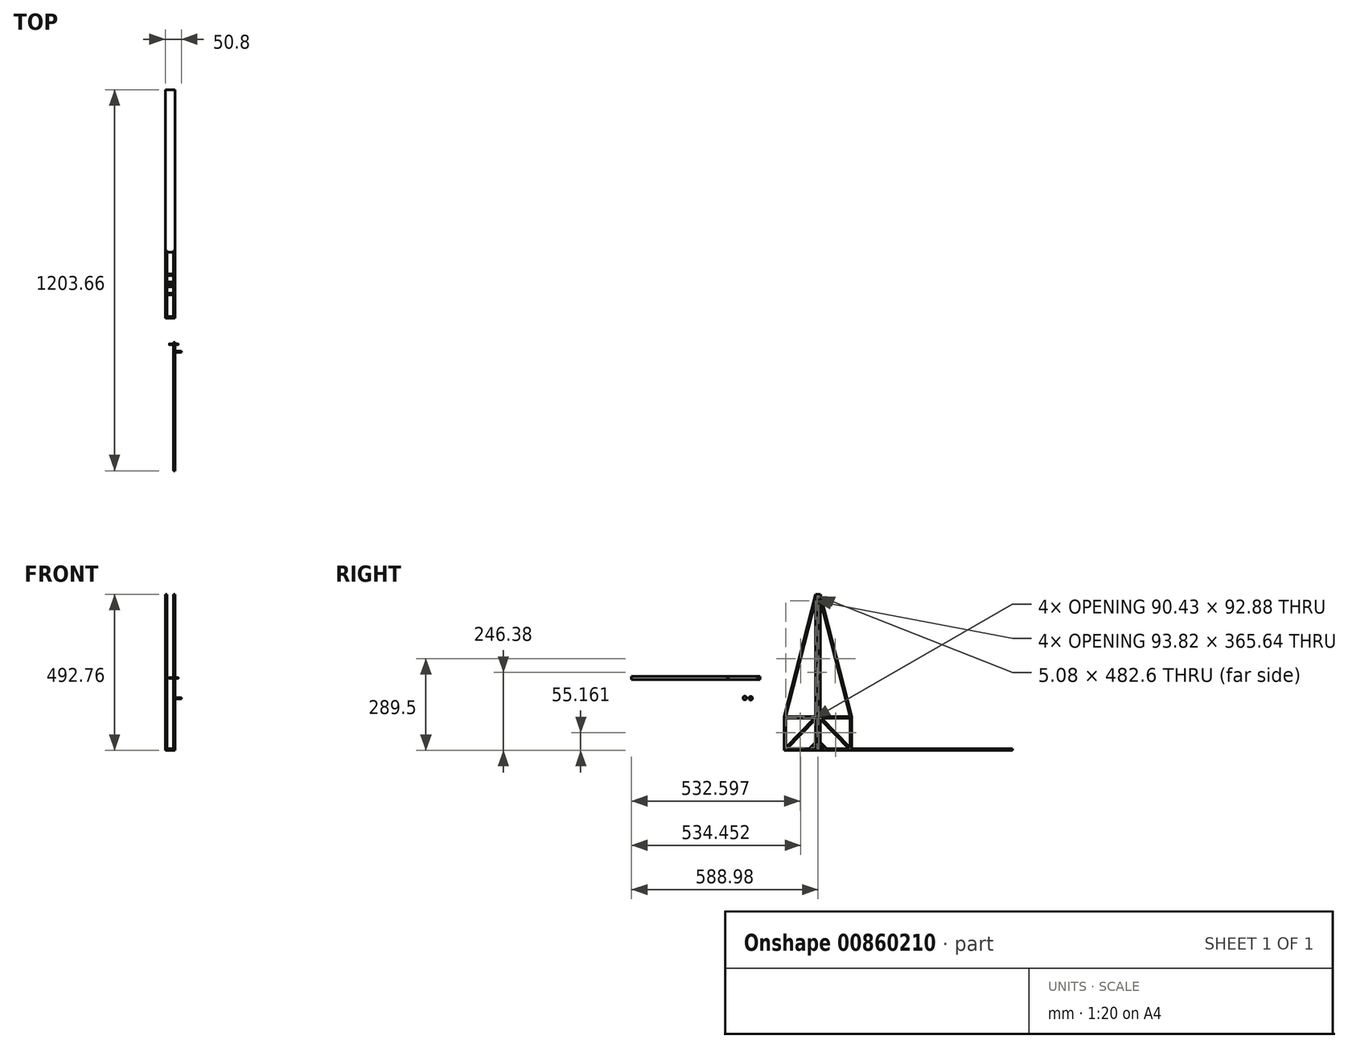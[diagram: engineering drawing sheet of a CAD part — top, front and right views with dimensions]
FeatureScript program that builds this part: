
annotation { "Feature Type Name" : "Feature", "Feature Type Description" : "" }
export const myFeature = defineFeature(function(context is Context, id is Id, definition is map)
    precondition{}
    {
        {
            var Q0;
            Q0=qCreatedBy(makeId("Right.planeOp"),FACE);
            var sketch = newSketch(context, id + "F0", { "sketchPlane" : qUnion([Q0])});
            skLineSegment(sketch, "E0.bottom", {"start": v(0, 0) * mm, "end": v(101.6, 0) * mm});
            skLineSegment(sketch, "E0.top", {"start": v(0, -101.6) * mm, "end": v(101.6, -101.6) * mm});
            skLineSegment(sketch, "E0.left", {"start": v(0, 0) * mm, "end": v(0, -101.6) * mm});
            skLineSegment(sketch, "E0.right", {"start": v(101.6, 0) * mm, "end": v(101.6, -101.6) * mm});
            skLineSegment(sketch, "E1.bottom", {"start": v(0, 0) * mm, "end": v(-101.6, 0) * mm});
            skLineSegment(sketch, "E1.top", {"start": v(0, -101.6) * mm, "end": v(-101.6, -101.6) * mm});
            skLineSegment(sketch, "E1.right", {"start": v(-101.6, 0) * mm, "end": v(-101.6, -101.6) * mm});
            skLineSegment(sketch, "E2.0", {"start": v(106.68, 0) * mm, "end": v(106.68, -106.68) * mm});
            skLineSegment(sketch, "E2.1", {"start": v(0, -106.68) * mm, "end": v(106.68, -106.68) * mm});
            skLineSegment(sketch, "E2.2", {"start": v(0, -106.68) * mm, "end": v(-106.68, -106.68) * mm});
            skLineSegment(sketch, "E2.3", {"start": v(-106.68, 0) * mm, "end": v(-106.68, -106.68) * mm});
            skLineSegment(sketch, "E3.0", {"start": v(0, -5.08) * mm, "end": v(101.6, -5.08) * mm});
            skLineSegment(sketch, "E3.1", {"start": v(0, -5.08) * mm, "end": v(-101.6, -5.08) * mm});
            skLineSegment(sketch, "E4", {"start": v(-106.68, 0) * mm, "end": v(-101.6, 0) * mm});
            skLineSegment(sketch, "E5", {"start": v(101.6, 0) * mm, "end": v(106.68, 0) * mm});
            skLineSegment(sketch, "E6.0", {"start": v(2.54, 0) * mm, "end": v(2.54, 381) * mm});
            skLineSegment(sketch, "E7.0", {"start": v(-2.54, 0) * mm, "end": v(-2.54, 381) * mm});
            skLineSegment(sketch, "E8", {"start": v(-2.54, 381) * mm, "end": v(2.54, 381) * mm});
            skLineSegment(sketch, "E9", {"start": v(2.54, 381) * mm, "end": v(7.62, 381) * mm});
            skLineSegment(sketch, "E10", {"start": v(7.62, 381) * mm, "end": v(7.62, 0) * mm});
            skLineSegment(sketch, "E11.0", {"start": v(-7.62, 0) * mm, "end": v(-7.62, 381) * mm});
            skLineSegment(sketch, "E12", {"start": v(-7.62, 381) * mm, "end": v(-2.54, 381) * mm});
            skLineSegment(sketch, "E13", {"start": v(-7.62, 381) * mm, "end": v(-7.62, 386.08) * mm});
            skLineSegment(sketch, "E14", {"start": v(-7.62, 386.08) * mm, "end": v(7.62, 386.08) * mm});
            skLineSegment(sketch, "E15", {"start": v(7.62, 386.08) * mm, "end": v(7.62, 381) * mm});
            skLineSegment(sketch, "E16", {"start": v(-2.54, 0) * mm, "end": v(-2.54, -101.6) * mm});
            skLineSegment(sketch, "E17", {"start": v(-7.62, 0) * mm, "end": v(-7.62, -101.6) * mm});
            skLineSegment(sketch, "E18", {"start": v(2.54, 0) * mm, "end": v(2.54, -101.6) * mm});
            skLineSegment(sketch, "E19", {"start": v(7.62, 0) * mm, "end": v(7.62, -101.6) * mm});
            skLineSegment(sketch, "E20", {"start": v(-7.62, -101.6) * mm, "end": v(-7.62, -88.9) * mm});
            skLineSegment(sketch, "E21", {"start": v(-7.62, -101.6) * mm, "end": v(-20.32, -101.6) * mm});
            skLineSegment(sketch, "E22", {"start": v(-20.32, -101.6) * mm, "end": v(-7.62, -88.9) * mm});
            skLineSegment(sketch, "E23.0", {"start": v(-23.91, -98) * mm, "end": v(-11.21, -85.3) * mm});
            skLineSegment(sketch, "E24", {"start": v(-23.91, -98) * mm, "end": v(-27.5, -101.6) * mm});
            skLineSegment(sketch, "E25", {"start": v(-11.21, -85.3) * mm, "end": v(-7.62, -81.72) * mm});
            skLineSegment(sketch, "E26.MirrorCS", {"start": v(23.91, -98) * mm, "end": v(27.5, -101.6) * mm});
            skLineSegment(sketch, "E27.MirrorCS", {"start": v(23.91, -98) * mm, "end": v(11.21, -85.3) * mm});
            skLineSegment(sketch, "E28.MirrorCS", {"start": v(20.32, -101.6) * mm, "end": v(7.62, -88.9) * mm});
            skLineSegment(sketch, "E29.MirrorCS", {"start": v(11.21, -85.3) * mm, "end": v(7.62, -81.72) * mm});
            skLineSegment(sketch, "E30", {"start": v(-7.62, 386.08) * mm, "end": v(-106.68, 0) * mm});
            skPoint(sketch, "E31", {"position": v(-7.62, 365.64) * mm});
            skPoint(sketch, "E32", {"position": v(-101.44, 0) * mm});
            skLineSegment(sketch, "E33", {"start": v(-101.44, 0) * mm, "end": v(-7.62, 365.64) * mm});
            skLineSegment(sketch, "E34.MirrorCS", {"start": v(101.44, 0) * mm, "end": v(7.62, 365.64) * mm});
            skLineSegment(sketch, "E35.MirrorCS", {"start": v(7.62, 386.08) * mm, "end": v(106.68, 0) * mm});
            skPoint(sketch, "E36", {"position": v(-101.6, -97.96) * mm});
            skPoint(sketch, "E37", {"position": v(-98.05, -101.6) * mm});
            skPoint(sketch, "E38", {"position": v(-7.62, -8.72) * mm});
            skPoint(sketch, "E39", {"position": v(-11.17, -5.08) * mm});
            skLineSegment(sketch, "E40", {"start": v(-7.62, -8.72) * mm, "end": v(-98.05, -101.6) * mm});
            skLineSegment(sketch, "E41", {"start": v(-101.6, -97.96) * mm, "end": v(-11.17, -5.08) * mm});
            skLineSegment(sketch, "E42.MirrorCS", {"start": v(101.6, -97.96) * mm, "end": v(11.17, -5.08) * mm});
            skLineSegment(sketch, "E43.MirrorCS", {"start": v(7.62, -8.72) * mm, "end": v(98.05, -101.6) * mm});
            skSolve(sketch);
        }
        {
            var Q0;
            Q0=makeQuery(id+"F0.imprint","IMPRINT",FACE,{"disambiguationData":[TD([[makeQuery(id+"F0.imprint","IMPRINT",EDGE,{"derivedFrom":sQuery(id+"F0.wireOp",EDGE,"E2.0")}),-1.0]])]});
            var Q1;
            {var subQ0=sQuery(id+"F0.wireOp",EDGE,"E3.0");var subQ1=sQuery(id+"F0.wireOp",EDGE,"E0.right");var subQ2=makeQuery(id+"F0.imprint","INTERSECT",VERTEX,{"derivedFrom":[subQ1,subQ0]});Q1=makeQuery(id+"F0.imprint","IMPRINT",FACE,{"disambiguationData":[TD([[makeQuery(id+"F0.imprint","IMPRINT",EDGE,{"disambiguationData":[TD([[subQ2,1.0]])],"derivedFrom":subQ0}),1.0]])]});}
            var Q2;
            {var subQ0=sQuery(id+"F0.wireOp",EDGE,"E3.1");var subQ1=sQuery(id+"F0.wireOp",EDGE,"E1.right");var subQ2=makeQuery(id+"F0.imprint","INTERSECT",VERTEX,{"derivedFrom":[subQ1,subQ0]});Q2=makeQuery(id+"F0.imprint","IMPRINT",FACE,{"disambiguationData":[TD([[makeQuery(id+"F0.imprint","IMPRINT",EDGE,{"disambiguationData":[TD([[subQ2,1.0]])],"derivedFrom":subQ0}),-1.0]])]});}
            var Q3;
            {var subQ4=sQuery(id+"F0.wireOp",EDGE,"E6.0");Q3=makeQuery(id+"F0.imprint","IMPRINT",FACE,{"disambiguationData":[TD([[makeQuery(id+"F0.imprint","IMPRINT",EDGE,{"derivedFrom":subQ4}),-1.0]])]});}
            var Q4;
            {var subQ5=sQuery(id+"F0.wireOp",EDGE,"E7.0");Q4=makeQuery(id+"F0.imprint","IMPRINT",FACE,{"disambiguationData":[TD([[makeQuery(id+"F0.imprint","IMPRINT",EDGE,{"derivedFrom":subQ5}),1.0]])]});}
            var Q5;
            Q5=makeQuery(id+"F0.imprint","IMPRINT",FACE,{"disambiguationData":[TD([[makeQuery(id+"F0.imprint","IMPRINT",EDGE,{"derivedFrom":sQuery(id+"F0.wireOp",EDGE,"E8")}),1.0]])]});
            var Q6;
            {var subQ3=sQuery(id+"F0.wireOp",EDGE,"E16");var subQ4=sQuery(id+"F0.wireOp",EDGE,"E1.top");var subQ5=makeQuery(id+"F0.imprint","INTERSECT",VERTEX,{"derivedFrom":[subQ4,subQ3]});Q6=makeQuery(id+"F0.imprint","IMPRINT",FACE,{"disambiguationData":[TD([[makeQuery(id+"F0.imprint","IMPRINT",EDGE,{"disambiguationData":[TD([[subQ5,-1.0]])],"derivedFrom":subQ4}),-1.0]])]});}
            var Q7;
            {var subQ0=sQuery(id+"F0.wireOp",EDGE,"E40");Q7=makeQuery(id+"F0.imprint","IMPRINT",FACE,{"disambiguationData":[TD([[makeQuery(id+"F0.imprint","IMPRINT",EDGE,{"derivedFrom":subQ0}),-1.0]])]});}
            var Q8;
            {var subQ3=sQuery(id+"F0.wireOp",EDGE,"E18");var subQ5=sQuery(id+"F0.wireOp",EDGE,"E3.0");var subQ7=makeQuery(id+"F0.imprint","INTERSECT",VERTEX,{"derivedFrom":[subQ5,subQ3]});Q8=makeQuery(id+"F0.imprint","IMPRINT",FACE,{"disambiguationData":[TD([[makeQuery(id+"F0.imprint","IMPRINT",EDGE,{"disambiguationData":[TD([[subQ7,-1.0]])],"derivedFrom":subQ5}),1.0]])]});}
            var Q9;
            {var subQ3=sQuery(id+"F0.wireOp",EDGE,"E16");var subQ5=sQuery(id+"F0.wireOp",EDGE,"E3.1");var subQ6=makeQuery(id+"F0.imprint","INTERSECT",VERTEX,{"derivedFrom":[subQ5,subQ3]});Q9=makeQuery(id+"F0.imprint","IMPRINT",FACE,{"disambiguationData":[TD([[makeQuery(id+"F0.imprint","IMPRINT",EDGE,{"disambiguationData":[TD([[subQ6,-1.0]])],"derivedFrom":subQ5}),-1.0]])]});}
            var Q10;
            {var subQ0=sQuery(id+"F0.wireOp",EDGE,"E18");var subQ1=sQuery(id+"F0.wireOp",EDGE,"E0.top");var subQ2=makeQuery(id+"F0.imprint","INTERSECT",VERTEX,{"derivedFrom":[subQ1,subQ0]});Q10=makeQuery(id+"F0.imprint","IMPRINT",FACE,{"disambiguationData":[TD([[makeQuery(id+"F0.imprint","IMPRINT",EDGE,{"disambiguationData":[TD([[subQ2,-1.0]])],"derivedFrom":subQ1}),1.0]])]});}
            var Q11;
            {var subQ4=sQuery(id+"F0.wireOp",EDGE,"E42.MirrorCS");Q11=makeQuery(id+"F0.imprint","IMPRINT",FACE,{"disambiguationData":[TD([[makeQuery(id+"F0.imprint","IMPRINT",EDGE,{"derivedFrom":subQ4}),1.0]])]});}
            var Q12;
            {var subQ0=sQuery(id+"F0.wireOp",EDGE,"E26.MirrorCS");Q12=makeQuery(id+"F0.imprint","IMPRINT",FACE,{"disambiguationData":[TD([[makeQuery(id+"F0.imprint","IMPRINT",EDGE,{"derivedFrom":subQ0}),-1.0]])]});}
            var Q13;
            {var subQ0=sQuery(id+"F0.wireOp",EDGE,"E22");Q13=makeQuery(id+"F0.imprint","IMPRINT",FACE,{"disambiguationData":[TD([[makeQuery(id+"F0.imprint","IMPRINT",EDGE,{"derivedFrom":subQ0}),1.0]])]});}
            var Q14;
            {var subQ3=sQuery(id+"F0.wireOp",EDGE,"E5");Q14=makeQuery(id+"F0.imprint","IMPRINT",FACE,{"disambiguationData":[TD([[makeQuery(id+"F0.imprint","IMPRINT",EDGE,{"derivedFrom":subQ3}),1.0]])]});}
            var Q15;
            {var subQ1=sQuery(id+"F0.wireOp",EDGE,"E4");Q15=makeQuery(id+"F0.imprint","IMPRINT",FACE,{"disambiguationData":[TD([[makeQuery(id+"F0.imprint","IMPRINT",EDGE,{"derivedFrom":subQ1}),1.0]])]});}
            extrude(context, id + "F1", {"entities" : qUnion([Q0, Q1, Q2, Q3, Q4, Q5, Q6, Q7, Q8, Q9, Q10, Q11, Q12, Q13, Q14, Q15]), "depth" : 5.08 * mm, "offsetDistance" : 25.4 * mm});
        }
        {
            var Q0;
            Q0=makeQuery(id+"F1.opExtrude","SWEPT_BODY",BODY,{"disambiguationData":[OSD([sQuery(id+"F0.wireOp",EDGE,"E0.bottom"),sQuery(id+"F0.wireOp",EDGE,"E0.top"),sQuery(id+"F0.wireOp",EDGE,"E0.right"),sQuery(id+"F0.wireOp",EDGE,"E1.bottom"),sQuery(id+"F0.wireOp",EDGE,"E1.top"),sQuery(id+"F0.wireOp",EDGE,"E1.right"),sQuery(id+"F0.wireOp",EDGE,"E2.0"),sQuery(id+"F0.wireOp",EDGE,"E2.1"),sQuery(id+"F0.wireOp",EDGE,"E2.2"),sQuery(id+"F0.wireOp",EDGE,"E2.3"),sQuery(id+"F0.wireOp",EDGE,"E3.0"),sQuery(id+"F0.wireOp",EDGE,"E3.1"),sQuery(id+"F0.wireOp",EDGE,"E6.0"),sQuery(id+"F0.wireOp",EDGE,"E7.0"),sQuery(id+"F0.wireOp",EDGE,"E8"),sQuery(id+"F0.wireOp",EDGE,"E10"),sQuery(id+"F0.wireOp",EDGE,"E11.0"),sQuery(id+"F0.wireOp",EDGE,"E14"),sQuery(id+"F0.wireOp",EDGE,"E16"),sQuery(id+"F0.wireOp",EDGE,"E17"),sQuery(id+"F0.wireOp",EDGE,"E18"),sQuery(id+"F0.wireOp",EDGE,"E19"),sQuery(id+"F0.wireOp",EDGE,"E22"),sQuery(id+"F0.wireOp",EDGE,"E23.0"),sQuery(id+"F0.wireOp",EDGE,"E24"),sQuery(id+"F0.wireOp",EDGE,"E25"),sQuery(id+"F0.wireOp",EDGE,"E26.MirrorCS"),sQuery(id+"F0.wireOp",EDGE,"E27.MirrorCS"),sQuery(id+"F0.wireOp",EDGE,"E28.MirrorCS"),sQuery(id+"F0.wireOp",EDGE,"E29.MirrorCS"),sQuery(id+"F0.wireOp",EDGE,"E30"),sQuery(id+"F0.wireOp",EDGE,"E33"),sQuery(id+"F0.wireOp",EDGE,"E34.MirrorCS"),sQuery(id+"F0.wireOp",EDGE,"E35.MirrorCS"),sQuery(id+"F0.wireOp",EDGE,"E40"),sQuery(id+"F0.wireOp",EDGE,"E41"),sQuery(id+"F0.wireOp",EDGE,"E42.MirrorCS"),sQuery(id+"F0.wireOp",EDGE,"E43.MirrorCS")])]});
            transform(context, id + "F2", {"entities" : qUnion([Q0]), "transformType" : TransformType.COPY});
        }
        {
            var Q0;
            Q0=makeQuery(id+"F2.opPattern","COPY",BODY,{"derivedFrom":makeQuery(id+"F1.opExtrude","SWEPT_BODY",BODY,{"disambiguationData":[OSD([sQuery(id+"F0.wireOp",EDGE,"E0.bottom"),sQuery(id+"F0.wireOp",EDGE,"E0.top"),sQuery(id+"F0.wireOp",EDGE,"E0.right"),sQuery(id+"F0.wireOp",EDGE,"E1.bottom"),sQuery(id+"F0.wireOp",EDGE,"E1.top"),sQuery(id+"F0.wireOp",EDGE,"E1.right"),sQuery(id+"F0.wireOp",EDGE,"E2.0"),sQuery(id+"F0.wireOp",EDGE,"E2.1"),sQuery(id+"F0.wireOp",EDGE,"E2.2"),sQuery(id+"F0.wireOp",EDGE,"E2.3"),sQuery(id+"F0.wireOp",EDGE,"E3.0"),sQuery(id+"F0.wireOp",EDGE,"E3.1"),sQuery(id+"F0.wireOp",EDGE,"E6.0"),sQuery(id+"F0.wireOp",EDGE,"E7.0"),sQuery(id+"F0.wireOp",EDGE,"E8"),sQuery(id+"F0.wireOp",EDGE,"E10"),sQuery(id+"F0.wireOp",EDGE,"E11.0"),sQuery(id+"F0.wireOp",EDGE,"E14"),sQuery(id+"F0.wireOp",EDGE,"E16"),sQuery(id+"F0.wireOp",EDGE,"E17"),sQuery(id+"F0.wireOp",EDGE,"E18"),sQuery(id+"F0.wireOp",EDGE,"E19"),sQuery(id+"F0.wireOp",EDGE,"E22"),sQuery(id+"F0.wireOp",EDGE,"E23.0"),sQuery(id+"F0.wireOp",EDGE,"E24"),sQuery(id+"F0.wireOp",EDGE,"E25"),sQuery(id+"F0.wireOp",EDGE,"E26.MirrorCS"),sQuery(id+"F0.wireOp",EDGE,"E27.MirrorCS"),sQuery(id+"F0.wireOp",EDGE,"E28.MirrorCS"),sQuery(id+"F0.wireOp",EDGE,"E29.MirrorCS"),sQuery(id+"F0.wireOp",EDGE,"E30"),sQuery(id+"F0.wireOp",EDGE,"E33"),sQuery(id+"F0.wireOp",EDGE,"E34.MirrorCS"),sQuery(id+"F0.wireOp",EDGE,"E35.MirrorCS"),sQuery(id+"F0.wireOp",EDGE,"E40"),sQuery(id+"F0.wireOp",EDGE,"E41"),sQuery(id+"F0.wireOp",EDGE,"E42.MirrorCS"),sQuery(id+"F0.wireOp",EDGE,"E43.MirrorCS")])]}),"instanceName":"1"});
            transform(context, id + "F3", {"entities" : qUnion([Q0]), "transformType" : TransformType.TRANSLATION_3D, "dx" : -25.4 * mm, "dy" : 0 * mm, "dz" : 0 * mm, "makeCopy" : false});
        }
        {
            var Q0;
            Q0=makeQuery(id+"F1.opExtrude","CAP_FACE",FACE,{"disambiguationData":[OSD([sQuery(id+"F0.wireOp",EDGE,"E0.bottom"),sQuery(id+"F0.wireOp",EDGE,"E0.top"),sQuery(id+"F0.wireOp",EDGE,"E0.right"),sQuery(id+"F0.wireOp",EDGE,"E1.bottom"),sQuery(id+"F0.wireOp",EDGE,"E1.top"),sQuery(id+"F0.wireOp",EDGE,"E1.right"),sQuery(id+"F0.wireOp",EDGE,"E2.0"),sQuery(id+"F0.wireOp",EDGE,"E2.1"),sQuery(id+"F0.wireOp",EDGE,"E2.2"),sQuery(id+"F0.wireOp",EDGE,"E2.3"),sQuery(id+"F0.wireOp",EDGE,"E3.0"),sQuery(id+"F0.wireOp",EDGE,"E3.1"),sQuery(id+"F0.wireOp",EDGE,"E6.0"),sQuery(id+"F0.wireOp",EDGE,"E7.0"),sQuery(id+"F0.wireOp",EDGE,"E8"),sQuery(id+"F0.wireOp",EDGE,"E10"),sQuery(id+"F0.wireOp",EDGE,"E11.0"),sQuery(id+"F0.wireOp",EDGE,"E14"),sQuery(id+"F0.wireOp",EDGE,"E16"),sQuery(id+"F0.wireOp",EDGE,"E17"),sQuery(id+"F0.wireOp",EDGE,"E18"),sQuery(id+"F0.wireOp",EDGE,"E19"),sQuery(id+"F0.wireOp",EDGE,"E22"),sQuery(id+"F0.wireOp",EDGE,"E23.0"),sQuery(id+"F0.wireOp",EDGE,"E24"),sQuery(id+"F0.wireOp",EDGE,"E25"),sQuery(id+"F0.wireOp",EDGE,"E26.MirrorCS"),sQuery(id+"F0.wireOp",EDGE,"E27.MirrorCS"),sQuery(id+"F0.wireOp",EDGE,"E28.MirrorCS"),sQuery(id+"F0.wireOp",EDGE,"E29.MirrorCS"),sQuery(id+"F0.wireOp",EDGE,"E30"),sQuery(id+"F0.wireOp",EDGE,"E33"),sQuery(id+"F0.wireOp",EDGE,"E34.MirrorCS"),sQuery(id+"F0.wireOp",EDGE,"E35.MirrorCS"),sQuery(id+"F0.wireOp",EDGE,"E40"),sQuery(id+"F0.wireOp",EDGE,"E41"),sQuery(id+"F0.wireOp",EDGE,"E42.MirrorCS"),sQuery(id+"F0.wireOp",EDGE,"E43.MirrorCS")])],"isStart":true});
            var sketch = newSketch(context, id + "F4", { "sketchPlane" : qUnion([Q0])});
            skLineSegment(sketch, "E44.bottom", {"start": v(-106.68, -106.68) * mm, "end": v(-101.6, -106.68) * mm});
            skLineSegment(sketch, "E44.top", {"start": v(-106.68, -101.6) * mm, "end": v(-101.6, -101.6) * mm});
            skLineSegment(sketch, "E44.left", {"start": v(-106.68, -106.68) * mm, "end": v(-106.68, -101.6) * mm});
            skLineSegment(sketch, "E44.right", {"start": v(-101.6, -106.68) * mm, "end": v(-101.6, -101.6) * mm});
            skLineSegment(sketch, "E45.bottom", {"start": v(106.68, -106.68) * mm, "end": v(101.6, -106.68) * mm});
            skLineSegment(sketch, "E45.top", {"start": v(106.68, -101.6) * mm, "end": v(101.6, -101.6) * mm});
            skLineSegment(sketch, "E45.left", {"start": v(106.68, -106.68) * mm, "end": v(106.68, -101.6) * mm});
            skLineSegment(sketch, "E45.right", {"start": v(101.6, -106.68) * mm, "end": v(101.6, -101.6) * mm});
            skLineSegment(sketch, "E46.bottom", {"start": v(-7.62, -101.6) * mm, "end": v(-2.54, -101.6) * mm});
            skLineSegment(sketch, "E46.top", {"start": v(-7.62, -106.68) * mm, "end": v(-2.54, -106.68) * mm});
            skLineSegment(sketch, "E46.left", {"start": v(-7.62, -101.6) * mm, "end": v(-7.62, -106.68) * mm});
            skLineSegment(sketch, "E46.right", {"start": v(-2.54, -101.6) * mm, "end": v(-2.54, -106.68) * mm});
            skLineSegment(sketch, "E47.bottom", {"start": v(2.54, -101.6) * mm, "end": v(7.62, -101.6) * mm});
            skLineSegment(sketch, "E47.top", {"start": v(2.54, -106.68) * mm, "end": v(7.62, -106.68) * mm});
            skLineSegment(sketch, "E47.left", {"start": v(2.54, -101.6) * mm, "end": v(2.54, -106.68) * mm});
            skLineSegment(sketch, "E47.right", {"start": v(7.62, -101.6) * mm, "end": v(7.62, -106.68) * mm});
            skLineSegment(sketch, "E48.bottom", {"start": v(27.5, -101.6) * mm, "end": v(32.58, -101.6) * mm});
            skLineSegment(sketch, "E48.top", {"start": v(27.5, -106.68) * mm, "end": v(32.58, -106.68) * mm});
            skLineSegment(sketch, "E48.left", {"start": v(27.5, -101.6) * mm, "end": v(27.5, -106.68) * mm});
            skLineSegment(sketch, "E48.right", {"start": v(32.58, -101.6) * mm, "end": v(32.58, -106.68) * mm});
            skLineSegment(sketch, "E49.bottom", {"start": v(-27.5, -101.6) * mm, "end": v(-32.58, -101.6) * mm});
            skLineSegment(sketch, "E49.top", {"start": v(-27.5, -106.68) * mm, "end": v(-32.58, -106.68) * mm});
            skLineSegment(sketch, "E49.left", {"start": v(-27.5, -101.6) * mm, "end": v(-27.5, -106.68) * mm});
            skLineSegment(sketch, "E49.right", {"start": v(-32.58, -101.6) * mm, "end": v(-32.58, -106.68) * mm});
            skSolve(sketch);
        }
        {
            var Q0;
            Q0=makeQuery(id+"F4.imprint","IMPRINT",FACE,{"disambiguationData":[TD([[makeQuery(id+"F4.imprint","IMPRINT",EDGE,{"derivedFrom":sQuery(id+"F4.wireOp",EDGE,"E44.bottom")}),1.0]])]});
            var Q1;
            Q1=makeQuery(id+"F4.imprint","IMPRINT",FACE,{"disambiguationData":[TD([[makeQuery(id+"F4.imprint","IMPRINT",EDGE,{"derivedFrom":sQuery(id+"F4.wireOp",EDGE,"E49.bottom")}),1.0]])]});
            var Q2;
            Q2=makeQuery(id+"F4.imprint","IMPRINT",FACE,{"disambiguationData":[TD([[makeQuery(id+"F4.imprint","IMPRINT",EDGE,{"derivedFrom":sQuery(id+"F4.wireOp",EDGE,"E46.bottom")}),-1.0]])]});
            var Q3;
            Q3=makeQuery(id+"F4.imprint","IMPRINT",FACE,{"disambiguationData":[TD([[makeQuery(id+"F4.imprint","IMPRINT",EDGE,{"derivedFrom":sQuery(id+"F4.wireOp",EDGE,"E47.bottom")}),-1.0]])]});
            var Q4;
            Q4=makeQuery(id+"F4.imprint","IMPRINT",FACE,{"disambiguationData":[TD([[makeQuery(id+"F4.imprint","IMPRINT",EDGE,{"derivedFrom":sQuery(id+"F4.wireOp",EDGE,"E48.bottom")}),-1.0]])]});
            var Q5;
            Q5=makeQuery(id+"F4.imprint","IMPRINT",FACE,{"disambiguationData":[TD([[makeQuery(id+"F4.imprint","IMPRINT",EDGE,{"derivedFrom":sQuery(id+"F4.wireOp",EDGE,"E45.bottom")}),1.0]])]});
            extrude(context, id + "F5", {"entities" : qUnion([Q0, Q1, Q2, Q3, Q4, Q5]), "operationType" : NewBodyOperationType.ADD, "endBound" : BoundingType.UP_TO_NEXT, "depth" : 25.4 * mm, "offsetDistance" : 25.4 * mm});
        }
        {
            var Q0;
            Q0=qCreatedBy(makeId("Right.planeOp"),FACE);
            var sketch = newSketch(context, id + "F6", { "sketchPlane" : qUnion([Q0])});
            skLineSegment(sketch, "E50.bottom", {"start": v(-182.58, 126.66) * mm, "end": v(-588.98, 126.66) * mm});
            skLineSegment(sketch, "E50.top", {"start": v(-182.58, 116.5) * mm, "end": v(-588.98, 116.5) * mm});
            skLineSegment(sketch, "E50.left", {"start": v(-182.58, 126.66) * mm, "end": v(-182.58, 116.5) * mm});
            skLineSegment(sketch, "E50.right", {"start": v(-588.98, 126.66) * mm, "end": v(-588.98, 116.5) * mm});
            skCircle(sketch, "E51", {"center": v(-284.18, 121.58) * mm, "radius": 1.59 * mm});
            skLineSegment(sketch, "E52", {"start": v(-187.66, 121.58) * mm, "end": v(-190.84, 121.58) * mm});
            skCircle(sketch, "E53", {"center": v(-189.25, 121.58) * mm, "radius": 1.59 * mm});
            skSolve(sketch);
        }
        {
            var Q0;
            Q0=makeQuery(id+"F6.imprint","IMPRINT",FACE,{"disambiguationData":[TD([[makeQuery(id+"F6.imprint","IMPRINT",EDGE,{"derivedFrom":sQuery(id+"F6.wireOp",EDGE,"E50.bottom")}),1.0]])]});
            var Q1;
            {var subQ0=sQuery(id+"F6.wireOp",EDGE,"E52");Q1=makeQuery(id+"F6.imprint","IMPRINT",FACE,{"disambiguationData":[TD([[makeQuery(id+"F6.imprint","IMPRINT",EDGE,{"derivedFrom":subQ0}),1.0]])]});}
            var Q2;
            {var subQ0=sQuery(id+"F6.wireOp",EDGE,"E52");Q2=makeQuery(id+"F6.imprint","IMPRINT",FACE,{"disambiguationData":[TD([[makeQuery(id+"F6.imprint","IMPRINT",EDGE,{"derivedFrom":subQ0}),-1.0]])]});}
            extrude(context, id + "F7", {"entities" : qUnion([Q0, Q1, Q2]), "depth" : 5.08 * mm, "offsetDistance" : 25.4 * mm});
        }
        {
            var Q0;
            Q0=qCreatedBy(makeId("Right.planeOp"),FACE);
            var sketch = newSketch(context, id + "F8", { "sketchPlane" : qUnion([Q0])});
            skCircle(sketch, "E54", {"center": v(-212.43, 57.86) * mm, "radius": 5.72 * mm});
            skCircle(sketch, "E55", {"center": v(-212.43, 57.86) * mm, "radius": 1.59 * mm});
            skSolve(sketch);
        }
        {
            var Q0;
            Q0=makeQuery(id+"F8.imprint","IMPRINT",FACE,{"disambiguationData":[TD([[makeQuery(id+"F8.imprint","IMPRINT",EDGE,{"derivedFrom":sQuery(id+"F8.wireOp",EDGE,"E54")}),1.0]])]});
            var Q1;
            Q1=makeQuery(id+"F8.imprint","IMPRINT",FACE,{"disambiguationData":[TD([[makeQuery(id+"F8.imprint","IMPRINT",EDGE,{"derivedFrom":sQuery(id+"F8.wireOp",EDGE,"E55")}),1.0]])]});
            extrude(context, id + "F9", {"entities" : qUnion([Q0, Q1]), "depth" : 2.54 * mm, "offsetDistance" : 25.4 * mm});
        }
        {
            var Q0;
            Q0=makeQuery(id+"F8.imprint","IMPRINT",FACE,{"disambiguationData":[TD([[makeQuery(id+"F8.imprint","IMPRINT",EDGE,{"derivedFrom":sQuery(id+"F8.wireOp",EDGE,"E55")}),1.0]])]});
            extrude(context, id + "F10", {"entities" : qUnion([Q0]), "operationType" : NewBodyOperationType.ADD, "depth" : 25.4 * mm, "offsetDistance" : 25.4 * mm});
        }
        {
            var Q0;
            Q0=qCreatedBy(makeId("Right.planeOp"),FACE);
            var sketch = newSketch(context, id + "F11", { "sketchPlane" : qUnion([Q0])});
            skCircle(sketch, "E56", {"center": v(-231.2, 58.48) * mm, "radius": 5.72 * mm});
            skSolve(sketch);
        }
        {
            var Q0;
            Q0=makeQuery(id+"F11.imprint","IMPRINT",FACE,{"disambiguationData":[TD([[makeQuery(id+"F11.imprint","IMPRINT",EDGE,{"derivedFrom":sQuery(id+"F11.wireOp",EDGE,"E56")}),1.0]])]});
            extrude(context, id + "F12", {"entities" : qUnion([Q0]), "depth" : 2.54 * mm, "offsetDistance" : 25.4 * mm});
        }
        {
            var Q0;
            Q0=qCreatedBy(makeId("Right.planeOp"),FACE);
            var sketch = newSketch(context, id + "F13", { "sketchPlane" : qUnion([Q0])});
            skCircle(sketch, "E57", {"center": v(-173.65, 60.41) * mm, "radius": 1.59 * mm});
            skSolve(sketch);
        }
        {
            var Q0;
            Q0=sQuery(id+"F13.wireOp",EDGE,"E57");
            extrude(context, id + "F14", {"bodyType" : ToolBodyType.SURFACE, "surfaceEntities" : qUnion([Q0]), "depth" : 40.64 * mm, "offsetDistance" : 25.4 * mm});
        }
        {
            var Q0;
            {var subQ0=sQuery(id+"F6.wireOp",EDGE,"E52");Q0=makeQuery(id+"F6.imprint","IMPRINT",FACE,{"disambiguationData":[TD([[makeQuery(id+"F6.imprint","IMPRINT",EDGE,{"derivedFrom":subQ0}),-1.0]])]});}
            var Q1;
            {var subQ0=sQuery(id+"F6.wireOp",EDGE,"E52");Q1=makeQuery(id+"F6.imprint","IMPRINT",FACE,{"disambiguationData":[TD([[makeQuery(id+"F6.imprint","IMPRINT",EDGE,{"derivedFrom":subQ0}),1.0]])]});}
            extrude(context, id + "F15", {"entities" : qUnion([Q0, Q1]), "operationType" : NewBodyOperationType.ADD, "depth" : 15.24 * mm, "offsetDistance" : 25.4 * mm});
        }
        {
            var Q0;
            {var subQ0=sQuery(id+"F6.wireOp",EDGE,"E52");Q0=makeQuery(id+"F6.imprint","IMPRINT",FACE,{"disambiguationData":[TD([[makeQuery(id+"F6.imprint","IMPRINT",EDGE,{"derivedFrom":subQ0}),-1.0]])]});}
            var Q1;
            {var subQ0=sQuery(id+"F6.wireOp",EDGE,"E52");Q1=makeQuery(id+"F6.imprint","IMPRINT",FACE,{"disambiguationData":[TD([[makeQuery(id+"F6.imprint","IMPRINT",EDGE,{"derivedFrom":subQ0}),1.0]])]});}
            extrude(context, id + "F16", {"entities" : qUnion([Q0, Q1]), "operationType" : NewBodyOperationType.ADD, "oppositeDirection" : true, "depth" : 12.7 * mm, "offsetDistance" : 25.4 * mm});
        }
        {
            var Q0;
            {var subQ0=makeQuery(id+"F1.opExtrude","SWEPT_FACE",FACE,{"disambiguationData":[OSD([sQuery(id+"F0.wireOp",EDGE,"E2.0")])]});Q0=makeQuery(id+"F5.boolean.opBoolean","MERGE",FACE,{"derivedFrom":[subQ0,makeQuery(id+"F2.opPattern","COPY",FACE,{"derivedFrom":subQ0,"instanceName":"1"}),makeQuery(id+"F5.opExtrude","SWEPT_FACE",FACE,{"disambiguationData":[OSD([sQuery(id+"F4.wireOp",EDGE,"E44.left")])]})]});}
            var sketch = newSketch(context, id + "F17", { "sketchPlane" : qUnion([Q0])});
            skLineSegment(sketch, "E58", {"start": v(-5.08, -101.6) * mm, "end": v(25.4, -101.6) * mm});
            skSolve(sketch);
        }
        {
            var Q0;
            {var subQ0=sQuery(id+"F17.wireOp",EDGE,"E58");var subQ1=sQuery(id+"F0.wireOp",EDGE,"E2.0");var subQ2=makeQuery(id+"F1.opExtrude","CAP_EDGE",EDGE,{"disambiguationData":[OSD([subQ1])],"isStart":false});var subQ4=makeQuery(id+"F1.opExtrude","CAP_EDGE",EDGE,{"disambiguationData":[OSD([subQ1])],"isStart":true});var subQ7=makeQuery(id+"F17.imprint","INTERSECT",VERTEX,{"derivedFrom":[subQ4,subQ0]});var subQ11=makeQuery(id+"F17.imprint","INTERSECT",VERTEX,{"derivedFrom":[subQ2,subQ0]});Q0=makeQuery(id+"F17.imprint","IMPRINT",FACE,{"disambiguationData":[TD([[makeQuery(id+"F17.imprint","IMPRINT",EDGE,{"disambiguationData":[TD([[subQ7,1.0],[subQ11,-1.0]])],"derivedFrom":subQ0}),-1.0]])]});}
            extrude(context, id + "F18", {"entities" : qUnion([Q0]), "operationType" : NewBodyOperationType.ADD, "depth" : 508 * mm, "offsetDistance" : 25.4 * mm});
        }
    });
